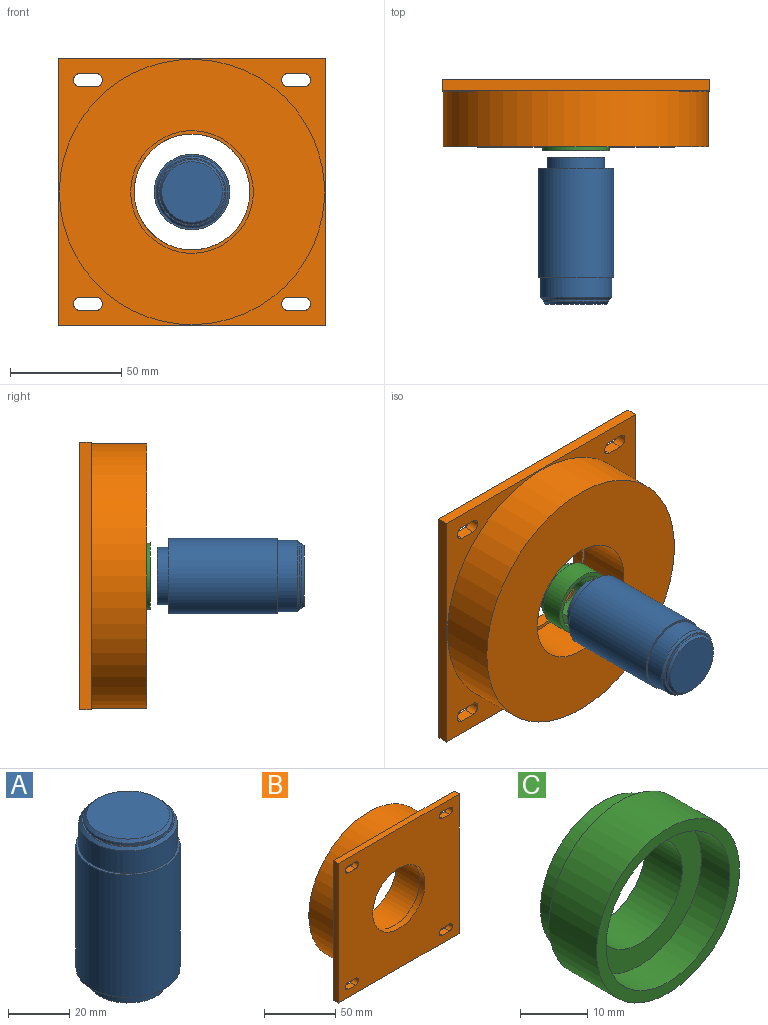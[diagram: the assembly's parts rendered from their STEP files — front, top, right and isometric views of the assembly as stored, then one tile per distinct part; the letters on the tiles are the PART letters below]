
ASSEMBLY  parts=3 mates=2
PART A: 11 faces, bbox 34x34x66 mm
  f0: cylinder r=17mm len=49mm, axis (0,0,-1), area 5233.9mm2, adj f2,f5
  f1: cylinder r=13mm len=26mm, axis (0,0,-1), area 408.4mm2, adj f2,f3
  f2: plane 34x34mm, normal (0,0,-1), area 377mm2, adj f0,f1
  f3: plane 26x26mm, normal (0,0,-1), area 530.9mm2, adj f1
  f4: cylinder r=16.1mm len=32.2mm, axis (0,0,1), area 910.4mm2, adj f5,f9
  f5: plane 34x34mm, normal (0,0,1), area 93.6mm2, adj f0,f4
  f6: plane 27.2x27.2mm, normal (0,0,1), area 581.1mm2, adj f10
  f7: cylinder r=14.6mm len=29.2mm, axis (0,0,1), area 91.7mm2, adj f8,f10
  f8: plane 30.2x30.2mm, normal (0,0,1), area 46.7mm2, adj f7,f9
  f9: cone r=15.1mm half-angle=45deg, axis (0,0,-1), area 138.6mm2, adj f4,f8
  f10: cone r=13.6mm half-angle=45deg, axis (0,0,-1), area 125.3mm2, adj f6,f7
PART B: 27 faces, bbox 120x30x120 mm
  f0: cylinder r=26mm len=52mm, axis (0,-1,0), area 816.8mm2, adj f22,f26
  f1: plane 120x5mm, normal (1,0,0), area 600mm2, adj f2,f4,f22,f24
  f2: plane 120x5mm, normal (0,0,1), area 600mm2, adj f1,f3,f22,f24
  f3: plane 120x5mm, normal (-1,0,0), area 600mm2, adj f2,f4,f22,f24
  f4: plane 120x5mm, normal (0,0,-1), area 600mm2, adj f1,f3,f22,f24
  f5: plane 119x119mm, normal (0,1,0), area 8746.2mm2, adj f23,f25
  f6: cylinder r=3mm len=6mm, axis (0,-1,0), area 47.1mm2, adj f7,f9,f22,f24
  f7: plane 7x5mm, normal (0,0,1), area 35mm2, adj f6,f8,f22,f24
  f8: cylinder r=3mm len=6mm, axis (0,-1,0), area 47.1mm2, adj f7,f9,f22,f24
  f9: plane 7x5mm, normal (0,0,-1), area 35mm2, adj f6,f8,f22,f24
  f10: cylinder r=3mm len=6mm, axis (0,-1,0), area 47.1mm2, adj f11,f13,f22,f24
  f11: plane 7x5mm, normal (0,0,-1), area 35mm2, adj f10,f12,f22,f24
  f12: cylinder r=3mm len=6mm, axis (0,-1,0), area 47.1mm2, adj f11,f13,f22,f24
  f13: plane 7x5mm, normal (0,0,1), area 35mm2, adj f10,f12,f22,f24
  f14: cylinder r=3mm len=6mm, axis (0,-1,0), area 47.1mm2, adj f15,f17,f22,f24
  f15: plane 7x5mm, normal (0,0,-1), area 35mm2, adj f14,f16,f22,f24
  f16: cylinder r=3mm len=6mm, axis (0,-1,0), area 47.1mm2, adj f15,f17,f22,f24
  f17: plane 7x5mm, normal (0,0,1), area 35mm2, adj f14,f16,f22,f24
  f18: cylinder r=3mm len=6mm, axis (0,-1,0), area 47.1mm2, adj f19,f21,f22,f24
  f19: plane 7x5mm, normal (0,0,1), area 35mm2, adj f18,f20,f22,f24
  f20: cylinder r=3mm len=6mm, axis (0,-1,0), area 47.1mm2, adj f19,f21,f22,f24
  f21: plane 7x5mm, normal (0,0,-1), area 35mm2, adj f18,f20,f22,f24
  f22: plane 120x120mm, normal (0,-1,0), area 11995.2mm2, adj f0,f1,f2,f3,f4,f6,f7,f8
  f23: cylinder r=59.5mm len=119mm, axis (0,1,0), area 9346.2mm2, adj f5,f24
  f24: plane 120x120mm, normal (0,1,0), area 2996.9mm2, adj f1,f2,f3,f4,f6,f7,f8,f9
  f25: cylinder r=27.5mm len=55mm, axis (0,1,0), area 4319.7mm2, adj f5,f26
  f26: plane 55x55mm, normal (0,1,0), area 252.1mm2, adj f0,f25
PART C: 8 faces, bbox 30x13.8x30 mm
  f0: cylinder r=9mm len=18mm, axis (0,-1,0), area 438.3mm2, adj f2,f6
  f1: cylinder r=15mm len=30mm, axis (0,-1,0), area 942.5mm2, adj f3,f5
  f2: plane 26x26mm, normal (0,1,0), area 276.5mm2, adj f0,f4
  f3: plane 30x30mm, normal (0,-1,0), area 175.9mm2, adj f1,f7
  f4: cylinder r=13mm len=26mm, axis (0,1,0), area 306.3mm2, adj f2,f5
  f5: plane 30x30mm, normal (0,1,0), area 175.9mm2, adj f1,f4
  f6: plane 26x26mm, normal (0,-1,0), area 276.5mm2, adj f0,f7
  f7: cylinder r=13mm len=26mm, axis (0,-1,0), area 490.1mm2, adj f3,f6
PLACE A rot(axis=(1,0,0),90deg) t=(-29.81,-57.49,38.26)mm
PLACE B rot(axis=(1,0,0),180deg) t=(-29.81,-22.88,38.26)mm
PLACE C t=(-29.81,-54.54,38.26)mm
MATE slider B.f0 <-> C.f4  axis (0,-1,0) through (-29.81,-27.88,38.26)mm
MATE slider A.f1 <-> B.f0  axis (0,1,0) through (-29.81,-57.49,38.26)mm
